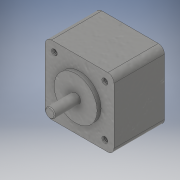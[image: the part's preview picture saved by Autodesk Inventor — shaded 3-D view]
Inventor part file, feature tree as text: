
AUTODESK INVENTOR PART (.ipt)
format: ipt  version: 2017 (Build 210142000, 142)  size: 592,896 bytes
history: native  units: in
note: dims shown in document units (in); Inventor stores cm internally (conversion verified against a paired STEP export)
features: chamfer x1, other x1
ambient origin geometry x8: Origin, YZ Plane, XZ Plane, XY Plane, X Axis, Y Axis, Z Axis, Center Point
bodies: Solid1 (feature_tree), Solid2 (feature_tree)
feature tree (2):
  chamfer  "Chamfer1"  [1 undecoded]
  other  "LPattern1"
note: 1 required parameter value undecoded (feature->parameter linkage not recoverable at this tier; creation-order binding heuristic only, values carry confidence <= 0.55)
